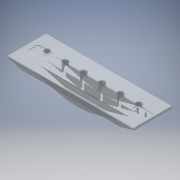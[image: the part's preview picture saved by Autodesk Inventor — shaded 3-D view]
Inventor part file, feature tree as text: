
AUTODESK INVENTOR PART (.ipt)
format: ipt  version: 2018.1 (Build 221171000, 171)  size: 459,264 bytes
history: native  units: in
note: dims shown in document units (in); Inventor stores cm internally (conversion verified against a paired STEP export)
features: sketch x5, extrude x4, fillet x3, pattern_linear x2, hole x2, chamfer x1
ambient origin geometry x8: Origin, YZ Plane, XZ Plane, XY Plane, X Axis, Y Axis, Z Axis, Center Point
bodies: Solid1 (feature_tree)
feature tree (17):
  extrude  "Extrusion1"  Depth=5.9055in
  sketch  "Sketch2"  dims[d2=5.9055in d3=0.0in d4=4.7244in]
  extrude  "Extrusion2"  Depth=4.7244in
  pattern_linear  "Rectangular Pattern1"  Count1=2  [1 undecoded]
  extrude  "Extrusion3"  Depth=0.3937in
  fillet  "Fillet1"  Radius=5.9055in
  fillet  "Fillet2"  [1 undecoded]
  extrude  "Extrusion4"  TaperAngle=15.0deg  [1 undecoded]
  fillet  "Fillet3"  Radius=5.9055in
  chamfer  "Chamfer1"  Distance=0.1969in
  hole  "Hole1"  [1 undecoded]
  hole  "Hole2"  [1 undecoded]
  pattern_linear  "Rectangular Pattern2"  Count1=6  [1 undecoded]
  sketch  "Sketch1"  dims[d0=21.6535in d1=5.9055in]
  sketch  "Sketch4"  dims[d5=0.3937in]
  sketch  "Sketch5"  dims[d6=0.1969in d7=0.7874in]
  sketch  "Sketch6"  dims[d9=5.9055in d10=0.0in d11=1.9685in d13=1.1811in d14=5.9055in d15=15.0deg d16=15.0deg d17=5.9055in d18=0.0in d19=0.1969in d20=0.1969in d21=0.7874in d22=2.3622in d23=0.1969in d24=2.3622in d25=1.5748in d26=0.7874in d27=0.0787in d28=0.0in d29=0.1969in d30=0.0394in d31=0.0787in d32=45.0deg d34=0.3937in d35=0.3937in d36=1.1811in d37=0.2362in d38=0.2362in d39=0.1575in d40=0.0787in d41=90.0deg d42=0.315in d43=0.8108in d60=0.3937in d61=0.3937in d46=0.7874in d47=0.2362in d48=0.9055in d49=0.0787in d50=90.0deg d51=0.315in d52=0.8108in d53=2.3622in d57=2.7559in]
note: 6 required parameter values undecoded (feature->parameter linkage not recoverable at this tier; creation-order binding heuristic only, values carry confidence <= 0.55)
